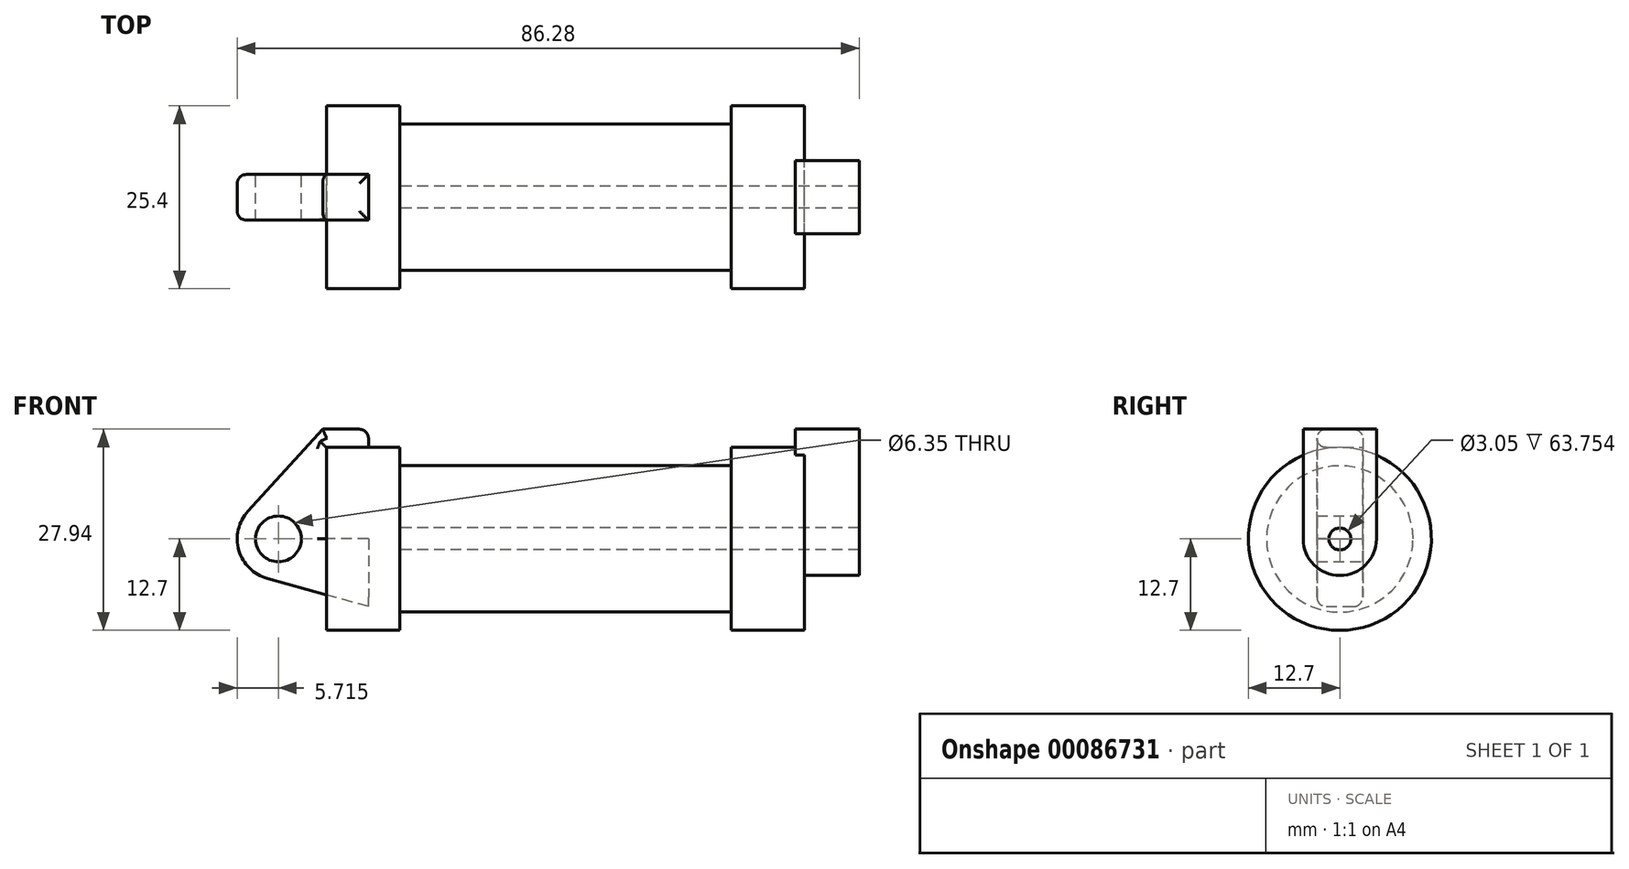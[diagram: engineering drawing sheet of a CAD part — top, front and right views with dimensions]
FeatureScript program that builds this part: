
annotation { "Feature Type Name" : "Feature", "Feature Type Description" : "" }
export const myFeature = defineFeature(function(context is Context, id is Id, definition is map)
    precondition{}
    {
        {
            var Q0;
            Q0=qCreatedBy(makeId("Front.planeOp"),FACE);
            var sketch = newSketch(context, id + "F0", { "sketchPlane" : qUnion([Q0])});
            skLineSegment(sketch, "E0", {"start": v(0, 0) * mm, "end": v(0, 12.7) * mm});
            skLineSegment(sketch, "E1", {"start": v(0, 12.7) * mm, "end": v(10.16, 12.7) * mm});
            skLineSegment(sketch, "E2", {"start": v(10.16, 12.7) * mm, "end": v(10.16, 10.16) * mm});
            skLineSegment(sketch, "E3", {"start": v(10.16, 10.16) * mm, "end": v(56.13, 10.16) * mm});
            skLineSegment(sketch, "E4", {"start": v(56.13, 10.16) * mm, "end": v(56.13, 12.7) * mm});
            skLineSegment(sketch, "E5", {"start": v(56.13, 12.7) * mm, "end": v(66.3, 12.7) * mm});
            skLineSegment(sketch, "E6", {"start": v(66.3, 12.7) * mm, "end": v(66.3, 0) * mm});
            skLineSegment(sketch, "E7", {"start": v(66.3, 0) * mm, "end": v(0, 0) * mm});
            skLineSegment(sketch, "E8", {"start": v(5.84, 15.24) * mm, "end": v(-0.5, 15.24) * mm});
            skLineSegment(sketch, "E9", {"start": v(-0.5, 15.24) * mm, "end": v(-10.88, 3.85) * mm});
            skLineSegment(sketch, "E10", {"start": v(0, 0) * mm, "end": v(-6.65, 0) * mm});
            skCircle(sketch, "E11", {"center": v(-6.65, 0) * mm, "radius": 5.72 * mm});
            skCircle(sketch, "E12", {"center": v(-6.65, 0) * mm, "radius": 3.18 * mm});
            skLineSegment(sketch, "E13", {"start": v(5.84, 15.24) * mm, "end": v(5.84, -9.4) * mm});
            skLineSegment(sketch, "E14", {"start": v(5.84, -9.4) * mm, "end": v(-8.18, -5.5) * mm});
            skSolve(sketch);
        }
        {
            var Q0;
            {var subQ0=sQuery(id+"F0.wireOp",EDGE,"E0");Q0=makeQuery(id+"F0.imprint","IMPRINT",FACE,{"disambiguationData":[TD([[makeQuery(id+"F0.imprint","IMPRINT",EDGE,{"derivedFrom":subQ0}),-1.0]])]});}
            var Q1;
            {var subQ0=sQuery(id+"F0.wireOp",EDGE,"E2");Q1=makeQuery(id+"F0.imprint","IMPRINT",FACE,{"disambiguationData":[TD([[makeQuery(id+"F0.imprint","IMPRINT",EDGE,{"derivedFrom":subQ0}),-1.0]])]});}
            var Q2;
            Q2=sQuery(id+"F0.wireOp",EDGE,"E7");
            revolve(context, id + "F1", {"entities" : qUnion([Q0, Q1]), "axis" : qUnion([Q2]), "revolveType" : RevolveType.FULL});
        }
        {
            var Q0;
            {var subQ3=sQuery(id+"F0.wireOp",EDGE,"E0");Q0=makeQuery(id+"F0.imprint","IMPRINT",FACE,{"disambiguationData":[TD([[makeQuery(id+"F0.imprint","IMPRINT",EDGE,{"derivedFrom":subQ3}),1.0]])]});}
            var Q1;
            {var subQ4=sQuery(id+"F0.wireOp",EDGE,"E12");Q1=makeQuery(id+"F0.imprint","IMPRINT",FACE,{"disambiguationData":[TD([[makeQuery(id+"F0.imprint","IMPRINT",EDGE,{"derivedFrom":subQ4}),-1.0]])]});}
            var Q2;
            {var subQ0=sQuery(id+"F0.wireOp",EDGE,"E14");Q2=makeQuery(id+"F0.imprint","IMPRINT",FACE,{"disambiguationData":[TD([[makeQuery(id+"F0.imprint","IMPRINT",EDGE,{"derivedFrom":subQ0}),-1.0]])]});}
            extrude(context, id + "F2", {"entities" : qUnion([Q0, Q1, Q2]), "endBound" : BoundingType.SYMMETRIC, "depth" : 6.35 * mm});
        }
        {
            var Q0;
            Q0=makeQuery(id+"F1.opRevolve","SWEPT_FACE",FACE,{"disambiguationData":[OSD([sQuery(id+"F0.wireOp",EDGE,"E6")])]});
            var sketch = newSketch(context, id + "F3", { "sketchPlane" : qUnion([Q0])});
            skCircle(sketch, "E15", {"center": v(0, 0) * mm, "radius": 1.52 * mm});
            skCircle(sketch, "E16", {"center": v(0, 0) * mm, "radius": 5.08 * mm});
            skLineSegment(sketch, "E17", {"start": v(5.08, 0) * mm, "end": v(5.08, 15.24) * mm});
            skLineSegment(sketch, "E18", {"start": v(-5.08, 0) * mm, "end": v(-5.08, 15.24) * mm});
            skLineSegment(sketch, "E19", {"start": v(-5.08, 15.24) * mm, "end": v(5.08, 15.24) * mm});
            skSolve(sketch);
        }
        {
            var Q0;
            Q0 = qSketchRegion(id + "F3", true);
            extrude(context, id + "F4", {"entities" : qUnion([Q0]), "operationType" : NewBodyOperationType.ADD, "depth" : 7.62 * mm});
        }
        {
            var Q0;
            Q0 = qSketchRegion(id + "F3", true);
            extrude(context, id + "F5", {"entities" : qUnion([Q0]), "operationType" : NewBodyOperationType.ADD, "oppositeDirection" : true, "depth" : 1.27 * mm});
        }
        {
            var Q0;
            Q0=makeQuery(id+"F4.boolean.opBoolean","SPLIT",FACE,{"disambiguationData":[TD([makeQuery(id+"F4.opExtrude","SWEPT_FACE",FACE,{"disambiguationData":[OSD([sQuery(id+"F3.wireOp",EDGE,"E15")])]})])],"derivedFrom":makeQuery(id+"F1.opRevolve","SWEPT_FACE",FACE,{"disambiguationData":[OSD([sQuery(id+"F0.wireOp",EDGE,"E6")])]})});
            var Q1;
            Q1=makeQuery(id+"F1.opRevolve","SWEPT_FACE",FACE,{"disambiguationData":[OSD([sQuery(id+"F0.wireOp",EDGE,"E2")])]});
            extrude(context, id + "F6", {"entities" : qUnion([Q0]), "operationType" : NewBodyOperationType.REMOVE, "endBound" : BoundingType.UP_TO_SURFACE, "oppositeDirection" : true, "endBoundEntityFace" : qUnion([Q1]), "depth" : 25.4 * mm});
        }
        {
            var Q0;
            Q0=makeQuery(id+"F2.opExtrude","CAP_EDGE",EDGE,{"disambiguationData":[OSD([sQuery(id+"F0.wireOp",EDGE,"E8")])],"isStart":false});
            var Q1;
            Q1=makeQuery(id+"F2.opExtrude","SWEPT_EDGE",EDGE,{"disambiguationData":[OSD([sQuery(id+"F0.wireOp",EDGE,"E8"),sQuery(id+"F0.wireOp",EDGE,"E13")])]});
            var Q2;
            Q2=makeQuery(id+"F2.opExtrude","CAP_EDGE",EDGE,{"disambiguationData":[OSD([sQuery(id+"F0.wireOp",EDGE,"E8")])],"isStart":true});
            var Q3;
            {var subQ0=sQuery(id+"F3.wireOp",EDGE,"E19");var subQ1=sQuery(id+"F3.wireOp",EDGE,"E18");Q3=makeQuery(id+"F5.boolean.opBoolean","MERGE",EDGE,{"derivedFrom":[makeQuery(id+"F4.opExtrude","SWEPT_EDGE",EDGE,{"disambiguationData":[OSD([subQ1,subQ0])]}),makeQuery(id+"F5.opExtrude","SWEPT_EDGE",EDGE,{"disambiguationData":[OSD([subQ1,subQ0])]})]});}
            var Q4;
            Q4=makeQuery(id+"F4.opExtrude","CAP_EDGE",EDGE,{"disambiguationData":[OSD([sQuery(id+"F3.wireOp",EDGE,"E19")])],"isStart":false});
            var Q5;
            {var subQ0=sQuery(id+"F3.wireOp",EDGE,"E19");var subQ1=sQuery(id+"F3.wireOp",EDGE,"E17");Q5=makeQuery(id+"F5.boolean.opBoolean","MERGE",EDGE,{"derivedFrom":[makeQuery(id+"F4.opExtrude","SWEPT_EDGE",EDGE,{"disambiguationData":[OSD([subQ1,subQ0])]}),makeQuery(id+"F5.opExtrude","SWEPT_EDGE",EDGE,{"disambiguationData":[OSD([subQ1,subQ0])]})]});}
            var Q6;
            Q6=makeQuery(id+"F5.opExtrude","CAP_EDGE",EDGE,{"disambiguationData":[OSD([sQuery(id+"F3.wireOp",EDGE,"E19")])],"isStart":false});
            var Q7;
            Q7=makeQuery(id+"F1.opRevolve","SWEPT_FACE",FACE,{"disambiguationData":[OSD([sQuery(id+"F0.wireOp",EDGE,"E1")])]});
            var Q8;
            Q8=makeQuery(id+"F2.opExtrude","CAP_EDGE",EDGE,{"disambiguationData":[OSD([sQuery(id+"F0.wireOp",EDGE,"E9")])],"isStart":false});
            var Q9;
            Q9=makeQuery(id+"F2.opExtrude","CAP_EDGE",EDGE,{"disambiguationData":[OSD([sQuery(id+"F0.wireOp",EDGE,"E9")])],"isStart":true});
            var Q10;
            Q10=makeQuery(id+"F2.opExtrude","SWEPT_EDGE",EDGE,{"disambiguationData":[OSD([sQuery(id+"F0.wireOp",EDGE,"E9"),sQuery(id+"F0.wireOp",EDGE,"E11")])]});
            var Q11;
            Q11=makeQuery(id+"F2.opExtrude","CAP_EDGE",EDGE,{"disambiguationData":[OSD([sQuery(id+"F0.wireOp",EDGE,"E11")])],"isStart":false});
            var Q12;
            Q12=makeQuery(id+"F2.opExtrude","CAP_EDGE",EDGE,{"disambiguationData":[OSD([sQuery(id+"F0.wireOp",EDGE,"E11")])],"isStart":true});
            var Q13;
            Q13=makeQuery(id+"F2.opExtrude","SWEPT_EDGE",EDGE,{"disambiguationData":[OSD([sQuery(id+"F0.wireOp",EDGE,"E11"),sQuery(id+"F0.wireOp",EDGE,"E14")])]});
            var Q14;
            Q14=makeQuery(id+"F2.opExtrude","CAP_EDGE",EDGE,{"disambiguationData":[OSD([sQuery(id+"F0.wireOp",EDGE,"E14")])],"isStart":false});
            var Q15;
            Q15=makeQuery(id+"F2.opExtrude","CAP_EDGE",EDGE,{"disambiguationData":[OSD([sQuery(id+"F0.wireOp",EDGE,"E14")])],"isStart":true});
            var Q16;
            Q16=makeQuery(id+"F1.opRevolve","SWEPT_EDGE",EDGE,{"disambiguationData":[OSD([sQuery(id+"F0.wireOp",EDGE,"E4"),sQuery(id+"F0.wireOp",EDGE,"E5")])]});
            var Q17;
            Q17=makeQuery(id+"F4.boolean.opBoolean","SPLIT",EDGE,{"disambiguationData":[OD(1.0)],"derivedFrom":makeQuery(id+"F1.opRevolve","SWEPT_EDGE",EDGE,{"disambiguationData":[OSD([sQuery(id+"F0.wireOp",EDGE,"E5"),sQuery(id+"F0.wireOp",EDGE,"E6")])]})});
            var Q18;
            Q18=makeQuery(id+"F4.opExtrude","CAP_EDGE",EDGE,{"disambiguationData":[OSD([sQuery(id+"F3.wireOp",EDGE,"E16")])],"isStart":false});
            var Q19;
            Q19=makeQuery(id+"F4.opExtrude","CAP_EDGE",EDGE,{"disambiguationData":[OSD([sQuery(id+"F3.wireOp",EDGE,"E17")])],"isStart":false});
            var Q20;
            Q20=makeQuery(id+"F4.opExtrude","CAP_EDGE",EDGE,{"disambiguationData":[OSD([sQuery(id+"F3.wireOp",EDGE,"E18")])],"isStart":false});
            var Q21;
            Q21=makeQuery(id+"F5.opExtrude","CAP_EDGE",EDGE,{"disambiguationData":[OSD([sQuery(id+"F3.wireOp",EDGE,"E17")])],"isStart":false});
            var Q22;
            Q22=makeQuery(id+"F1.opRevolve","SWEPT_EDGE",EDGE,{"disambiguationData":[OSD([sQuery(id+"F0.wireOp",EDGE,"E1"),sQuery(id+"F0.wireOp",EDGE,"E2")])]});
            var Q23;
            {var subQ0=sQuery(id+"F3.wireOp",EDGE,"E16");var subQ1=sQuery(id+"F3.wireOp",EDGE,"E18");Q23=makeQuery(id+"F4.boolean.opBoolean","SPLIT",EDGE,{"disambiguationData":[TD([makeQuery(id+"F4.opExtrude","SWEPT_FACE",FACE,{"disambiguationData":[OSD([subQ0])]})])],"derivedFrom":makeQuery(id+"F4.opExtrude","CAP_EDGE",EDGE,{"disambiguationData":[OSD([subQ1])],"isStart":true})});}
            var Q24;
            Q24=makeQuery(id+"F4.opExtrude","SWEPT_EDGE",EDGE,{"disambiguationData":[OSD([sQuery(id+"F3.wireOp",EDGE,"E16"),sQuery(id+"F3.wireOp",EDGE,"E18")])]});
            var Q25;
            Q25=makeQuery(id+"F4.opExtrude","CAP_EDGE",EDGE,{"disambiguationData":[OSD([sQuery(id+"F3.wireOp",EDGE,"E16")])],"isStart":true});
            var Q26;
            {var subQ0=sQuery(id+"F3.wireOp",EDGE,"E16");var subQ1=sQuery(id+"F3.wireOp",EDGE,"E17");Q26=makeQuery(id+"F4.boolean.opBoolean","SPLIT",EDGE,{"disambiguationData":[TD([makeQuery(id+"F4.opExtrude","SWEPT_FACE",FACE,{"disambiguationData":[OSD([subQ0])]})])],"derivedFrom":makeQuery(id+"F4.opExtrude","CAP_EDGE",EDGE,{"disambiguationData":[OSD([subQ1])],"isStart":true})});}
            var Q27;
            Q27=makeQuery(id+"F5.opExtrude","CAP_EDGE",EDGE,{"disambiguationData":[OSD([sQuery(id+"F3.wireOp",EDGE,"E18")])],"isStart":false});
            var Q28;
            Q28=makeQuery(id+"F2.opExtrude","CAP_EDGE",EDGE,{"disambiguationData":[OSD([sQuery(id+"F0.wireOp",EDGE,"E0")])],"isStart":false});
            var Q29;
            Q29=makeQuery(id+"F2.opExtrude","CAP_EDGE",EDGE,{"disambiguationData":[OSD([sQuery(id+"F0.wireOp",EDGE,"E1")])],"isStart":false});
            fillet(context, id + "F7", {"entities" : qUnion([Q0, Q1, Q2, Q3, Q4, Q5, Q6, Q7, Q8, Q9, Q10, Q11, Q12, Q13, Q14, Q15, Q16, Q17, Q18, Q19, Q20, Q21, Q22, Q23, Q24, Q25, Q26, Q27, Q28, Q29]), "radius" : 1.27 * mm, "tangentPropagation" : true, "allowEdgeOverflow" : false});
        }
    });
